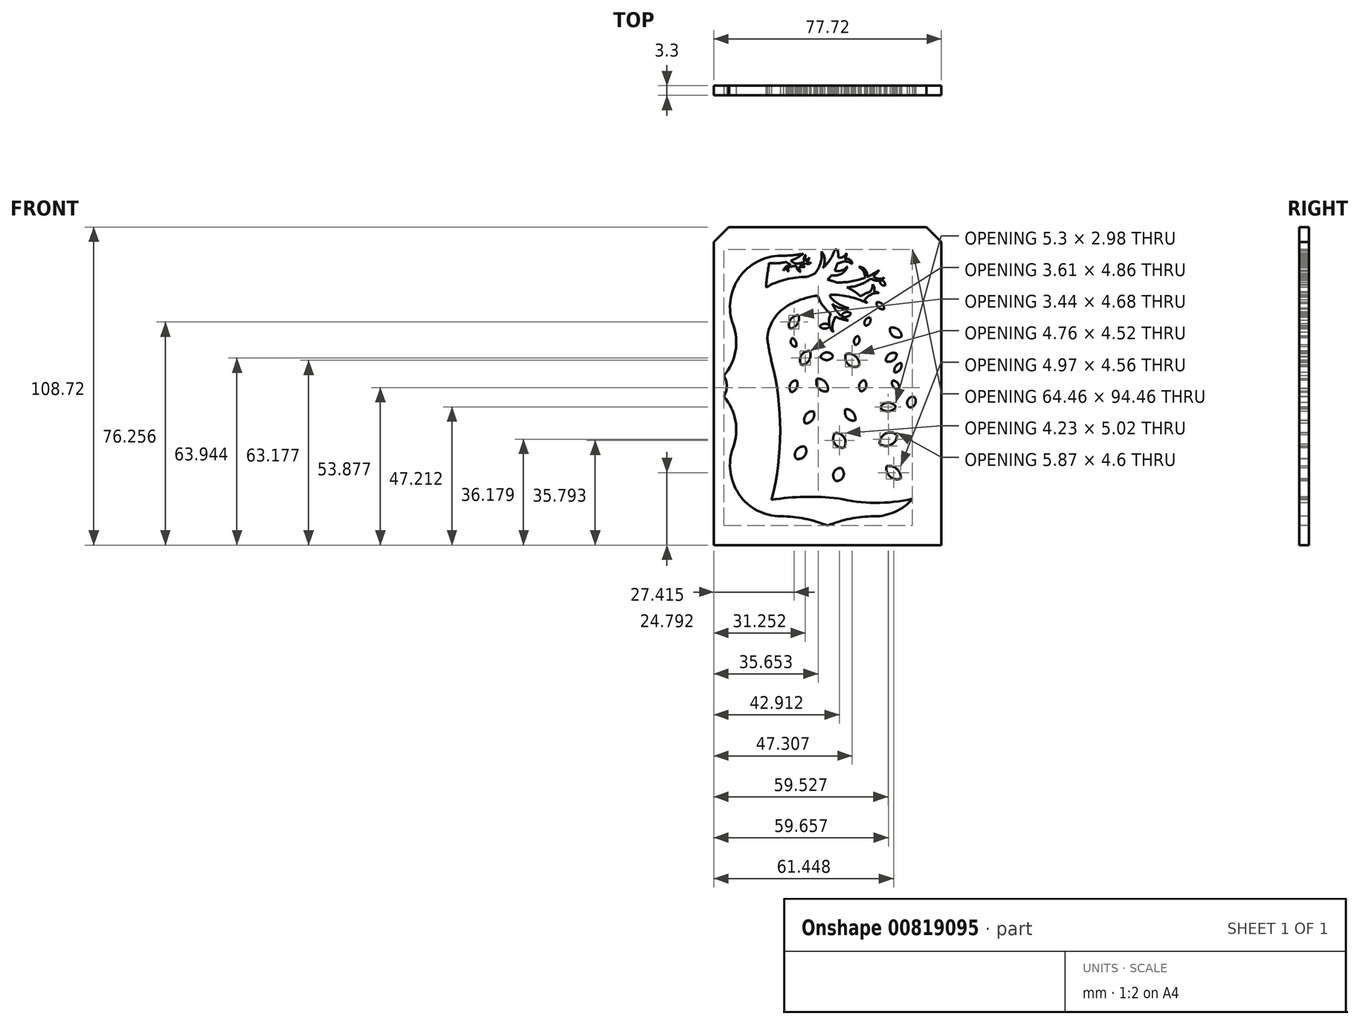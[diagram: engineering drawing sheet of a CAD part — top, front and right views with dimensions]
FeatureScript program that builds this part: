
annotation { "Feature Type Name" : "Feature", "Feature Type Description" : "" }
export const myFeature = defineFeature(function(context is Context, id is Id, definition is map)
    precondition{}
    {
        {
            var Q0;
            Q0=qCreatedBy(makeId("Front.planeOp"),FACE);
            var sketch = newSketch(context, id + "F0", { "sketchPlane" : qUnion([Q0])});
            skLineSegment(sketch, "E0.bottom", {"start": v(38.86, 54.36) * mm, "end": v(-38.86, 54.36) * mm});
            skLineSegment(sketch, "E0.top", {"start": v(38.86, -54.36) * mm, "end": v(-38.86, -54.36) * mm});
            skLineSegment(sketch, "E0.left", {"start": v(38.86, 54.36) * mm, "end": v(38.86, -54.36) * mm});
            skLineSegment(sketch, "E0.right", {"start": v(-38.86, 54.36) * mm, "end": v(-38.86, -54.36) * mm});
            skPoint(sketch, "E0.middle", {"position": v(0, 0) * mm});
            skSolve(sketch);
        }
        {
            var Q0;
            Q0=qSketchRegion(id+"F0",true);
            extrude(context, id + "F1", {"entities" : qUnion([Q0]), "depth" : 3.3 * mm});
        }
        {
            var Q0;
            Q0=makeQuery(id+"F1.opExtrude","CAP_FACE",FACE,{"disambiguationData":[OSD([sQuery(id+"F0.wireOp",EDGE,"E0.bottom"),sQuery(id+"F0.wireOp",EDGE,"E0.top"),sQuery(id+"F0.wireOp",EDGE,"E0.left"),sQuery(id+"F0.wireOp",EDGE,"E0.right")])],"isStart":false});
            var sketch = newSketch(context, id + "F2", { "sketchPlane" : qUnion([Q0])});
            skLineSegment(sketch, "E1", {"start": v(0, 57.24) * mm, "end": v(0, -57.24) * mm, "construction": true});
            skLineSegment(sketch, "E2", {"start": v(-50.8, 0) * mm, "end": v(50.8, 0) * mm, "construction": true});
            skArc(sketch, "E3", {"start": v(35.44, -3.57) * mm, "mid": v(31.46, -11.87) * mm, "end": v(32.26, -21.03) * mm});
            skLineSegment(sketch, "E4", {"start": v(15.88, -44.54) * mm, "end": v(0, -44.54) * mm, "construction": true});
            skArc(sketch, "E5", {"start": v(15.88, -44.54) * mm, "mid": v(30.2, -37.06) * mm, "end": v(32.26, -21.03) * mm});
            skArc(sketch, "E6", {"start": v(15.88, -44.54) * mm, "mid": v(7.78, -45.34) * mm, "end": v(0, -47.71) * mm});
            skArc(sketch, "E7.MirrorCS", {"start": v(-15.87, -44.54) * mm, "mid": v(-7.78, -45.34) * mm, "end": v(0, -47.71) * mm});
            skArc(sketch, "E8.MirrorCS", {"start": v(-15.87, -44.54) * mm, "mid": v(-30.2, -37.06) * mm, "end": v(-32.26, -21.03) * mm});
            skArc(sketch, "E9.MirrorCS", {"start": v(-35.44, -3.57) * mm, "mid": v(-31.46, -11.87) * mm, "end": v(-32.26, -21.03) * mm});
            skArc(sketch, "E10.MirrorCS", {"start": v(-35.44, 3.57) * mm, "mid": v(-31.46, 11.87) * mm, "end": v(-32.26, 21.03) * mm});
            skArc(sketch, "E11.MirrorCS", {"start": v(-15.88, 44.54) * mm, "mid": v(-30.2, 37.06) * mm, "end": v(-32.26, 21.03) * mm});
            skArc(sketch, "E12.MirrorCS", {"start": v(-15.88, 44.54) * mm, "mid": v(-7.78, 45.34) * mm, "end": v(0, 47.71) * mm});
            skArc(sketch, "E13.MirrorCS", {"start": v(15.87, 44.54) * mm, "mid": v(7.78, 45.34) * mm, "end": v(0, 47.71) * mm});
            skArc(sketch, "E14.MirrorCS", {"start": v(15.87, 44.54) * mm, "mid": v(30.2, 37.06) * mm, "end": v(32.26, 21.03) * mm});
            skArc(sketch, "E15.MirrorCS", {"start": v(35.44, 3.57) * mm, "mid": v(31.46, 11.87) * mm, "end": v(32.26, 21.03) * mm});
            skArc(sketch, "E16", {"start": v(35.44, 3.57) * mm, "mid": v(34.41, 0) * mm, "end": v(35.44, -3.57) * mm});
            skPoint(sketch, "E17.orphan", {"position": v(39.69, 0) * mm});
            skArc(sketch, "E18.MirrorCS", {"start": v(-35.44, 3.57) * mm, "mid": v(-34.41, 0) * mm, "end": v(-35.44, -3.57) * mm});
            skPoint(sketch, "E19.orphan", {"position": v(-39.69, 0) * mm});
            skSolve(sketch);
        }
        {
            var Q0;
            Q0=makeQuery(id+"F1.opExtrude","SWEPT_EDGE",EDGE,{"disambiguationData":[OSD([sQuery(id+"F0.wireOp",EDGE,"E0.bottom"),sQuery(id+"F0.wireOp",EDGE,"E0.right")])]});
            var Q1;
            Q1=makeQuery(id+"F1.opExtrude","SWEPT_EDGE",EDGE,{"disambiguationData":[OSD([sQuery(id+"F0.wireOp",EDGE,"E0.bottom"),sQuery(id+"F0.wireOp",EDGE,"E0.left")])]});
            chamfer(context, id + "F3", {"entities" : qUnion([Q0, Q1]), "width" : 5.08 * mm, "tangentPropagation" : true});
        }
        {
            var Q0;
            Q0=makeQuery(id+"F2.imprint","IMPRINT",FACE,{"disambiguationData":[TD([[makeQuery(id+"F2.imprint","IMPRINT",EDGE,{"derivedFrom":sQuery(id+"F2.wireOp",EDGE,"E3")}),-1.0]])]});
            var sketch = newSketch(context, id + "F4", { "sketchPlane" : qUnion([Q0])});
            skArc(sketch, "E20", {"start": v(3.54, -38.35) * mm, "mid": v(-7.8, -37.86) * mm, "end": v(-19.12, -38.87) * mm});
            skArc(sketch, "E21", {"start": v(3.54, -38.35) * mm, "mid": v(16.27, -39.9) * mm, "end": v(29.02, -38.57) * mm});
            skArc(sketch, "E22", {"start": v(-19.12, -38.87) * mm, "mid": v(-16.15, -15.26) * mm, "end": v(-19.12, 8.35) * mm});
            skArc(sketch, "E23", {"start": v(-11.74, 28.43) * mm, "mid": v(-17.82, 23.65) * mm, "end": v(-20.6, 16.43) * mm});
            skArc(sketch, "E24", {"start": v(13.5, 28.43) * mm, "mid": v(7.34, 30.55) * mm, "end": v(0.88, 31.26) * mm});
            skArc(sketch, "E25", {"start": v(13.5, 28.43) * mm, "mid": v(13.1, 28.9) * mm, "end": v(12.68, 29.37) * mm});
            skArc(sketch, "E26", {"start": v(2.96, 35.45) * mm, "mid": v(1.5, 35.96) * mm, "end": v(0, 36.4) * mm});
            skArc(sketch, "E27", {"start": v(6.63, 33.75) * mm, "mid": v(10.98, 34.65) * mm, "end": v(14.87, 36.8) * mm});
            skArc(sketch, "E28", {"start": v(2.96, 35.45) * mm, "mid": v(7.95, 35.75) * mm, "end": v(12.77, 37.06) * mm});
            skPoint(sketch, "E28.startSnap0", {"position": v(12.77, 35.45) * mm});
            skArc(sketch, "E29", {"start": v(-3.37, 30.96) * mm, "mid": v(-1.6, 27.49) * mm, "end": v(1.14, 24.74) * mm});
            skArc(sketch, "E30", {"start": v(0.88, 31.26) * mm, "mid": v(0.93, 30.8) * mm, "end": v(1, 30.35) * mm});
            skArc(sketch, "E31", {"start": v(-7.2, 37.31) * mm, "mid": v(-5.72, 37.81) * mm, "end": v(-4.31, 38.47) * mm});
            skArc(sketch, "E32", {"start": v(0, 36.4) * mm, "mid": v(0.74, 37.12) * mm, "end": v(1.4, 37.91) * mm});
            skArc(sketch, "E33", {"start": v(13.53, 37.37) * mm, "mid": v(12.87, 39.74) * mm, "end": v(10.62, 40.74) * mm});
            skPoint(sketch, "E33.endSnap0", {"position": v(10.62, 36.34) * mm});
            skArc(sketch, "E34", {"start": v(12.77, 37.06) * mm, "mid": v(12.3, 39.25) * mm, "end": v(10.62, 40.74) * mm});
            skArc(sketch, "E35", {"start": v(15.63, 37.44) * mm, "mid": v(17.43, 36.7) * mm, "end": v(19.35, 37) * mm});
            skArc(sketch, "E36", {"start": v(14.87, 36.8) * mm, "mid": v(16.36, 36.06) * mm, "end": v(18.03, 36.17) * mm});
            skArc(sketch, "E37", {"start": v(17.6, 31.9) * mm, "mid": v(16.78, 32.1) * mm, "end": v(15.95, 32.2) * mm});
            skArc(sketch, "E38", {"start": v(17.6, 31.9) * mm, "mid": v(14.82, 31.25) * mm, "end": v(12.68, 29.37) * mm});
            skArc(sketch, "E39", {"start": v(1.14, 24.74) * mm, "mid": v(0.5, 22.73) * mm, "end": v(0.67, 20.63) * mm});
            skArc(sketch, "E40", {"start": v(2.82, 23.7) * mm, "mid": v(1.73, 21.15) * mm, "end": v(1.97, 18.38) * mm});
            skArc(sketch, "E41", {"start": v(14.33, 32.08) * mm, "mid": v(15.18, 33.3) * mm, "end": v(15.4, 34.77) * mm});
            skArc(sketch, "E42", {"start": v(15.95, 32.2) * mm, "mid": v(16, 33.55) * mm, "end": v(15.4, 34.77) * mm});
            skArc(sketch, "E43", {"start": v(1.65, 28.14) * mm, "mid": v(4.24, 26.7) * mm, "end": v(7.21, 26.67) * mm});
            skArc(sketch, "E44", {"start": v(1, 30.35) * mm, "mid": v(3.82, 28.03) * mm, "end": v(7.21, 26.67) * mm});
            skArc(sketch, "E45", {"start": v(-1.61, 40.35) * mm, "mid": v(-0.98, 43.3) * mm, "end": v(-2.07, 46.1) * mm});
            skArc(sketch, "E46", {"start": v(-4.31, 38.47) * mm, "mid": v(-2.38, 42.05) * mm, "end": v(-2.07, 46.1) * mm});
            skArc(sketch, "E47", {"start": v(3.63, 43.86) * mm, "mid": v(5.33, 44.2) * mm, "end": v(6.52, 45.46) * mm});
            skArc(sketch, "E48", {"start": v(3.34, 41.94) * mm, "mid": v(3.95, 42.04) * mm, "end": v(4.53, 42.26) * mm});
            skArc(sketch, "E49", {"start": v(8.46, 41.73) * mm, "mid": v(7.59, 43.22) * mm, "end": v(5.87, 43.38) * mm});
            skArc(sketch, "E50", {"start": v(8.46, 41.73) * mm, "mid": v(6.53, 42.56) * mm, "end": v(4.46, 42.23) * mm});
            skArc(sketch, "E51", {"start": v(2.42, 39.5) * mm, "mid": v(4.84, 39.52) * mm, "end": v(6.82, 40.92) * mm});
            skArc(sketch, "E52", {"start": v(1.4, 37.91) * mm, "mid": v(4.7, 38.37) * mm, "end": v(6.82, 40.92) * mm});
            skArc(sketch, "E53", {"start": v(-19.9, 42.09) * mm, "mid": v(-17.02, 42) * mm, "end": v(-14.17, 42.41) * mm});
            skArc(sketch, "E54", {"start": v(-8.2, 45.26) * mm, "mid": v(-9.13, 44.66) * mm, "end": v(-10.04, 44.02) * mm});
            skArc(sketch, "E55", {"start": v(-14.17, 42.41) * mm, "mid": v(-13.33, 41.87) * mm, "end": v(-12.44, 41.43) * mm});
            skArc(sketch, "E56", {"start": v(-12.57, 42.88) * mm, "mid": v(-11.85, 42.33) * mm, "end": v(-11.08, 41.86) * mm});
            skArc(sketch, "E57", {"start": v(-10.44, 40.85) * mm, "mid": v(-10.15, 39.65) * mm, "end": v(-9.1, 39.01) * mm});
            skArc(sketch, "E58", {"start": v(-9.46, 40.74) * mm, "mid": v(-9.55, 39.82) * mm, "end": v(-9.1, 39.01) * mm});
            skArc(sketch, "E59", {"start": v(-11.08, 41.86) * mm, "mid": v(-9.44, 41.98) * mm, "end": v(-7.9, 42.55) * mm});
            skArc(sketch, "E60", {"start": v(-9.46, 41.18) * mm, "mid": v(-8.42, 41.43) * mm, "end": v(-7.5, 41.97) * mm});
            skArc(sketch, "E61", {"start": v(-6.97, 42.46) * mm, "mid": v(-6.36, 42.08) * mm, "end": v(-5.66, 42.21) * mm});
            skArc(sketch, "E62", {"start": v(-7.5, 41.97) * mm, "mid": v(-6.53, 41.75) * mm, "end": v(-5.66, 42.21) * mm});
            skArc(sketch, "E63", {"start": v(-7.37, 44.84) * mm, "mid": v(-8.05, 43.79) * mm, "end": v(-7.9, 42.55) * mm});
            skArc(sketch, "E64", {"start": v(-7.37, 44.84) * mm, "mid": v(-7.6, 43.85) * mm, "end": v(-7.37, 42.87) * mm});
            skArc(sketch, "E65", {"start": v(-12.44, 41.43) * mm, "mid": v(-14.1, 40.86) * mm, "end": v(-15.13, 39.43) * mm});
            skArc(sketch, "E66", {"start": v(-11.1, 40.99) * mm, "mid": v(-12.2, 40.91) * mm, "end": v(-13.27, 40.62) * mm});
            skArc(sketch, "E67", {"start": v(-13.6, 40.48) * mm, "mid": v(-13.82, 39.72) * mm, "end": v(-13.27, 39.14) * mm});
            skPoint(sketch, "E67.endSnap0", {"position": v(-13.27, 40.62) * mm});
            skArc(sketch, "E68", {"start": v(-13.27, 40.62) * mm, "mid": v(-13.44, 39.88) * mm, "end": v(-13.27, 39.14) * mm});
            skArc(sketch, "E69", {"start": v(0.67, 20.63) * mm, "mid": v(-1.07, 21.32) * mm, "end": v(-2.67, 20.36) * mm});
            skArc(sketch, "E70", {"start": v(-2.67, 20.36) * mm, "mid": v(-0.96, 19.6) * mm, "end": v(0.75, 20.36) * mm});
            skArc(sketch, "E71", {"start": v(8.04, 24.84) * mm, "mid": v(6.15, 25.25) * mm, "end": v(4.72, 23.96) * mm});
            skArc(sketch, "E72", {"start": v(18.03, 36.17) * mm, "mid": v(18.3, 34.78) * mm, "end": v(19.68, 34.44) * mm});
            skArc(sketch, "E73", {"start": v(19.68, 34.44) * mm, "mid": v(19.3, 35.65) * mm, "end": v(18.17, 36.22) * mm});
            skArc(sketch, "E74", {"start": v(4.89, 23.82) * mm, "mid": v(6.67, 23.7) * mm, "end": v(8.04, 24.84) * mm});
            skArc(sketch, "E75", {"start": v(16.76, 28.64) * mm, "mid": v(17.42, 26.84) * mm, "end": v(19.27, 26.32) * mm});
            skArc(sketch, "E76", {"start": v(19.27, 26.32) * mm, "mid": v(18.6, 28.12) * mm, "end": v(16.76, 28.64) * mm});
            skArc(sketch, "E77", {"start": v(14.47, 23.44) * mm, "mid": v(12.86, 22.48) * mm, "end": v(12.92, 20.6) * mm});
            skArc(sketch, "E78", {"start": v(12.92, 20.6) * mm, "mid": v(14.46, 21.6) * mm, "end": v(14.47, 23.44) * mm});
            skArc(sketch, "E79", {"start": v(-9.85, 24.24) * mm, "mid": v(-12.65, 22.73) * mm, "end": v(-12.86, 19.55) * mm});
            skArc(sketch, "E80", {"start": v(-12.86, 19.55) * mm, "mid": v(-10.32, 21.23) * mm, "end": v(-9.85, 24.24) * mm});
            skArc(sketch, "E81", {"start": v(21.34, 19.91) * mm, "mid": v(22.4, 17.15) * mm, "end": v(25.34, 16.9) * mm});
            skArc(sketch, "E82", {"start": v(25.34, 16.9) * mm, "mid": v(24.07, 19.38) * mm, "end": v(21.34, 19.91) * mm});
            skArc(sketch, "E83.trimOffspring", {"start": v(11.4, 30.63) * mm, "mid": v(9.13, 32.37) * mm, "end": v(6.63, 33.75) * mm});
            skArc(sketch, "E84.trimOffspring", {"start": v(14.33, 32.08) * mm, "mid": v(12.77, 31.54) * mm, "end": v(11.4, 30.63) * mm});
            skArc(sketch, "E85.trimOffspring", {"start": v(1.65, 28.14) * mm, "mid": v(2.93, 25.86) * mm, "end": v(4.72, 23.96) * mm});
            skArc(sketch, "E86.trimOffspring", {"start": v(-3.37, 30.96) * mm, "mid": v(-7.65, 30) * mm, "end": v(-11.74, 28.43) * mm});
            skArc(sketch, "E87.trimOffspring", {"start": v(2.82, 23.7) * mm, "mid": v(4.92, 22.87) * mm, "end": v(7.14, 22.42) * mm});
            skArc(sketch, "E88.trimOffspring", {"start": v(4.89, 23.82) * mm, "mid": v(5.97, 23.05) * mm, "end": v(7.14, 22.42) * mm});
            skArc(sketch, "E89.trimOffspring", {"start": v(0.75, 20.36) * mm, "mid": v(1.25, 19.3) * mm, "end": v(1.97, 18.38) * mm});
            skArc(sketch, "E90.trimOffspring", {"start": v(13.53, 37.37) * mm, "mid": v(15.63, 38.38) * mm, "end": v(17.62, 39.6) * mm});
            skArc(sketch, "E91.trimOffspring", {"start": v(15.63, 37.44) * mm, "mid": v(16.68, 38.46) * mm, "end": v(17.62, 39.6) * mm});
            skArc(sketch, "E92.trimOffspring", {"start": v(18.17, 36.22) * mm, "mid": v(18.8, 36.55) * mm, "end": v(19.35, 37) * mm});
            skArc(sketch, "E93.trimOffspring", {"start": v(2.42, 39.5) * mm, "mid": v(2.95, 40.69) * mm, "end": v(3.34, 41.94) * mm});
            skArc(sketch, "E94.trimOffspring", {"start": v(3.63, 43.86) * mm, "mid": v(3.64, 45.16) * mm, "end": v(3.5, 46.44) * mm});
            skArc(sketch, "E95.trimOffspring", {"start": v(5.87, 43.38) * mm, "mid": v(6.36, 44.36) * mm, "end": v(6.52, 45.46) * mm});
            skArc(sketch, "E96.trimOffspring", {"start": v(-1.61, 40.35) * mm, "mid": v(0.9, 43.27) * mm, "end": v(2.55, 46.75) * mm});
            skArc(sketch, "E97.trimOffspring", {"start": v(-7.2, 37.31) * mm, "mid": v(-14.34, 36.4) * mm, "end": v(-21.03, 33.75) * mm});
            skArc(sketch, "E98.trimOffspring", {"start": v(-20.6, 16.43) * mm, "mid": v(-19.97, 12.37) * mm, "end": v(-19.12, 8.35) * mm});
            skArc(sketch, "E99.trimOffspring", {"start": v(-11.1, 40.99) * mm, "mid": v(-10.77, 40.91) * mm, "end": v(-10.44, 40.85) * mm});
            skArc(sketch, "E100.trimOffspring", {"start": v(-13.6, 40.48) * mm, "mid": v(-14.4, 40.02) * mm, "end": v(-15.13, 39.43) * mm});
            skArc(sketch, "E101.trimOffspring", {"start": v(-9.46, 40.74) * mm, "mid": v(-8.58, 40.74) * mm, "end": v(-7.7, 40.82) * mm});
            skArc(sketch, "E102.trimOffspring", {"start": v(-9.46, 41.18) * mm, "mid": v(-8.6, 40.96) * mm, "end": v(-7.7, 40.82) * mm});
            skArc(sketch, "E103.trimOffspring", {"start": v(-6.97, 42.46) * mm, "mid": v(-6.5, 43.15) * mm, "end": v(-6.18, 43.93) * mm});
            skArc(sketch, "E104.trimOffspring", {"start": v(-7.37, 42.87) * mm, "mid": v(-6.74, 43.36) * mm, "end": v(-6.18, 43.93) * mm});
            skArc(sketch, "E105.trimOffspring", {"start": v(-12.57, 42.88) * mm, "mid": v(-11.28, 43.4) * mm, "end": v(-10.04, 44.02) * mm});
            skArc(sketch, "E106.0", {"start": v(15.88, -44.54) * mm, "mid": v(23.1, -42.98) * mm, "end": v(29.02, -38.57) * mm});
            skArc(sketch, "E107.0", {"start": v(15.88, -44.54) * mm, "mid": v(7.78, -45.34) * mm, "end": v(0, -47.71) * mm});
            skArc(sketch, "E108.0", {"start": v(-15.87, -44.54) * mm, "mid": v(-7.78, -45.34) * mm, "end": v(0, -47.71) * mm});
            skArc(sketch, "E109.0", {"start": v(-15.87, -44.54) * mm, "mid": v(-30.2, -37.06) * mm, "end": v(-32.26, -21.03) * mm});
            skArc(sketch, "E110.0", {"start": v(-35.44, -3.57) * mm, "mid": v(-31.46, -11.87) * mm, "end": v(-32.26, -21.03) * mm});
            skArc(sketch, "E111.0", {"start": v(-35.44, 3.57) * mm, "mid": v(-34.41, 0) * mm, "end": v(-35.44, -3.57) * mm});
            skArc(sketch, "E112.0", {"start": v(-35.44, 3.57) * mm, "mid": v(-31.46, 11.87) * mm, "end": v(-32.26, 21.03) * mm});
            skArc(sketch, "E113.0", {"start": v(-15.88, 44.54) * mm, "mid": v(-30.2, 37.06) * mm, "end": v(-32.26, 21.03) * mm});
            skArc(sketch, "E114.0", {"start": v(-15.88, 44.54) * mm, "mid": v(-12.02, 44.72) * mm, "end": v(-8.2, 45.26) * mm});
            skArc(sketch, "E115.0", {"start": v(3.5, 46.44) * mm, "mid": v(3.02, 46.6) * mm, "end": v(2.55, 46.75) * mm});
            skArc(sketch, "E116.trimOffspring", {"start": v(-19.9, 42.09) * mm, "mid": v(-20.57, 37.94) * mm, "end": v(-21.03, 33.75) * mm});
            skPoint(sketch, "E117.start.orphan", {"position": v(-19.12, 45.77) * mm});
            skPoint(sketch, "E118.orphan", {"position": v(0, 47.71) * mm});
            skPoint(sketch, "E119.orphan", {"position": v(2.96, 48.4) * mm});
            skPoint(sketch, "E120.orphan", {"position": v(15.87, 44.54) * mm});
            skPoint(sketch, "E121.orphan", {"position": v(32.26, -21.03) * mm});
            skPoint(sketch, "E122.orphan", {"position": v(29.98, -38.35) * mm});
            skArc(sketch, "E123", {"start": v(-6.09, 12.01) * mm, "mid": v(-8.99, 10.45) * mm, "end": v(-8.9, 7.16) * mm});
            skArc(sketch, "E124", {"start": v(-8.9, 7.16) * mm, "mid": v(-6.27, 8.87) * mm, "end": v(-6.09, 12.01) * mm});
            skArc(sketch, "E125", {"start": v(6.3, 10.96) * mm, "mid": v(7.13, 7.35) * mm, "end": v(10.8, 6.94) * mm});
            skArc(sketch, "E126", {"start": v(10.8, 6.94) * mm, "mid": v(9.63, 10.16) * mm, "end": v(6.3, 10.96) * mm});
            skArc(sketch, "E127", {"start": v(23.64, 11.09) * mm, "mid": v(21, 10.88) * mm, "end": v(19.98, 8.45) * mm});
            skArc(sketch, "E128", {"start": v(19.98, 8.45) * mm, "mid": v(22.5, 8.82) * mm, "end": v(23.64, 11.09) * mm});
            skArc(sketch, "E129", {"start": v(10.43, 17.1) * mm, "mid": v(9.1, 15.82) * mm, "end": v(9.54, 14.04) * mm});
            skArc(sketch, "E130", {"start": v(9.54, 14.04) * mm, "mid": v(10.86, 15.31) * mm, "end": v(10.43, 17.1) * mm});
            skArc(sketch, "E131", {"start": v(-12.06, 16.41) * mm, "mid": v(-12.41, 14.5) * mm, "end": v(-10.76, 13.47) * mm});
            skArc(sketch, "E132", {"start": v(-10.76, 13.47) * mm, "mid": v(-10.84, 15.2) * mm, "end": v(-12.06, 16.41) * mm});
            skArc(sketch, "E133", {"start": v(-3.64, 2.46) * mm, "mid": v(-3.1, -0.76) * mm, "end": v(0, -1.78) * mm});
            skArc(sketch, "E134", {"start": v(0, -1.78) * mm, "mid": v(-0.7, 1.3) * mm, "end": v(-3.64, 2.46) * mm});
            skArc(sketch, "E135", {"start": v(12.53, 2.05) * mm, "mid": v(10.87, 0.4) * mm, "end": v(11.4, -1.87) * mm});
            skArc(sketch, "E136", {"start": v(11.4, -1.87) * mm, "mid": v(13.16, -0.26) * mm, "end": v(12.53, 2.05) * mm});
            skArc(sketch, "E137", {"start": v(22.26, 1.96) * mm, "mid": v(22.43, -0.21) * mm, "end": v(24.5, -0.86) * mm});
            skArc(sketch, "E138", {"start": v(24.5, -0.86) * mm, "mid": v(23.96, 1) * mm, "end": v(22.26, 1.96) * mm});
            skArc(sketch, "E139", {"start": v(-4.74, -8.64) * mm, "mid": v(-7.44, -9.83) * mm, "end": v(-7.65, -12.77) * mm});
            skArc(sketch, "E140", {"start": v(-7.65, -12.77) * mm, "mid": v(-5.1, -11.48) * mm, "end": v(-4.74, -8.64) * mm});
            skArc(sketch, "E141", {"start": v(23.32, -7.15) * mm, "mid": v(20.59, -5.66) * mm, "end": v(18.02, -7.4) * mm});
            skArc(sketch, "E142", {"start": v(18.02, -7.4) * mm, "mid": v(20.73, -8.64) * mm, "end": v(23.32, -7.15) * mm});
            skArc(sketch, "E143", {"start": v(6.17, -7.89) * mm, "mid": v(6.6, -10.84) * mm, "end": v(9.47, -11.7) * mm});
            skArc(sketch, "E144", {"start": v(9.47, -11.7) * mm, "mid": v(8.72, -9.02) * mm, "end": v(6.17, -7.89) * mm});
            skArc(sketch, "E145", {"start": v(-10.57, 1.93) * mm, "mid": v(-12.78, 0.45) * mm, "end": v(-12.34, -2.17) * mm});
            skArc(sketch, "E146", {"start": v(-12.34, -2.17) * mm, "mid": v(-10.53, -0.52) * mm, "end": v(-10.57, 1.93) * mm});
            skArc(sketch, "E147", {"start": v(1.9, 10.13) * mm, "mid": v(-0.34, 11.52) * mm, "end": v(-2.4, 9.86) * mm});
            skArc(sketch, "E148", {"start": v(-2.4, 9.86) * mm, "mid": v(-0.18, 8.88) * mm, "end": v(1.9, 10.13) * mm});
            skArc(sketch, "E149", {"start": v(29.59, -3.68) * mm, "mid": v(27.38, -4.88) * mm, "end": v(28, -7.3) * mm});
            skArc(sketch, "E150", {"start": v(28, -7.3) * mm, "mid": v(29.98, -6.02) * mm, "end": v(29.59, -3.68) * mm});
            skArc(sketch, "E151", {"start": v(25.13, 7.95) * mm, "mid": v(23.3, 6.76) * mm, "end": v(22.85, 4.62) * mm});
            skArc(sketch, "E152", {"start": v(22.85, 4.62) * mm, "mid": v(24.84, 5.7) * mm, "end": v(25.13, 7.95) * mm});
            skArc(sketch, "E153", {"start": v(23.73, -16.7) * mm, "mid": v(19.74, -16.28) * mm, "end": v(17.86, -19.83) * mm});
            skArc(sketch, "E154", {"start": v(17.86, -19.83) * mm, "mid": v(21.75, -20.04) * mm, "end": v(23.73, -16.7) * mm});
            skArc(sketch, "E155", {"start": v(2.6, -16.06) * mm, "mid": v(2.4, -19.6) * mm, "end": v(5.65, -21.04) * mm});
            skArc(sketch, "E156", {"start": v(5.65, -21.04) * mm, "mid": v(5.69, -17.59) * mm, "end": v(2.6, -16.06) * mm});
            skArc(sketch, "E157", {"start": v(-7.7, -20.74) * mm, "mid": v(-10.57, -21.76) * mm, "end": v(-10.82, -24.79) * mm});
            skArc(sketch, "E158", {"start": v(-10.82, -24.79) * mm, "mid": v(-7.81, -23.88) * mm, "end": v(-7.7, -20.74) * mm});
            skArc(sketch, "E159", {"start": v(20.2, -27.34) * mm, "mid": v(21.35, -30.94) * mm, "end": v(25.07, -31.64) * mm});
            skArc(sketch, "E160", {"start": v(25.07, -31.64) * mm, "mid": v(23.66, -28.32) * mm, "end": v(20.2, -27.34) * mm});
            skArc(sketch, "E161", {"start": v(4.6, -28.03) * mm, "mid": v(2.13, -29.6) * mm, "end": v(2.86, -32.43) * mm});
            skArc(sketch, "E162", {"start": v(2.86, -32.43) * mm, "mid": v(5.4, -30.9) * mm, "end": v(4.6, -28.03) * mm});
            skSolve(sketch);
        }
        {
            var Q0;
            Q0=qSketchRegion(id+"F4",true);
            extrude(context, id + "F5", {"entities" : qUnion([Q0]), "operationType" : NewBodyOperationType.REMOVE, "endBound" : BoundingType.THROUGH_ALL, "oppositeDirection" : true, "depth" : 25.4 * mm});
        }
    });
